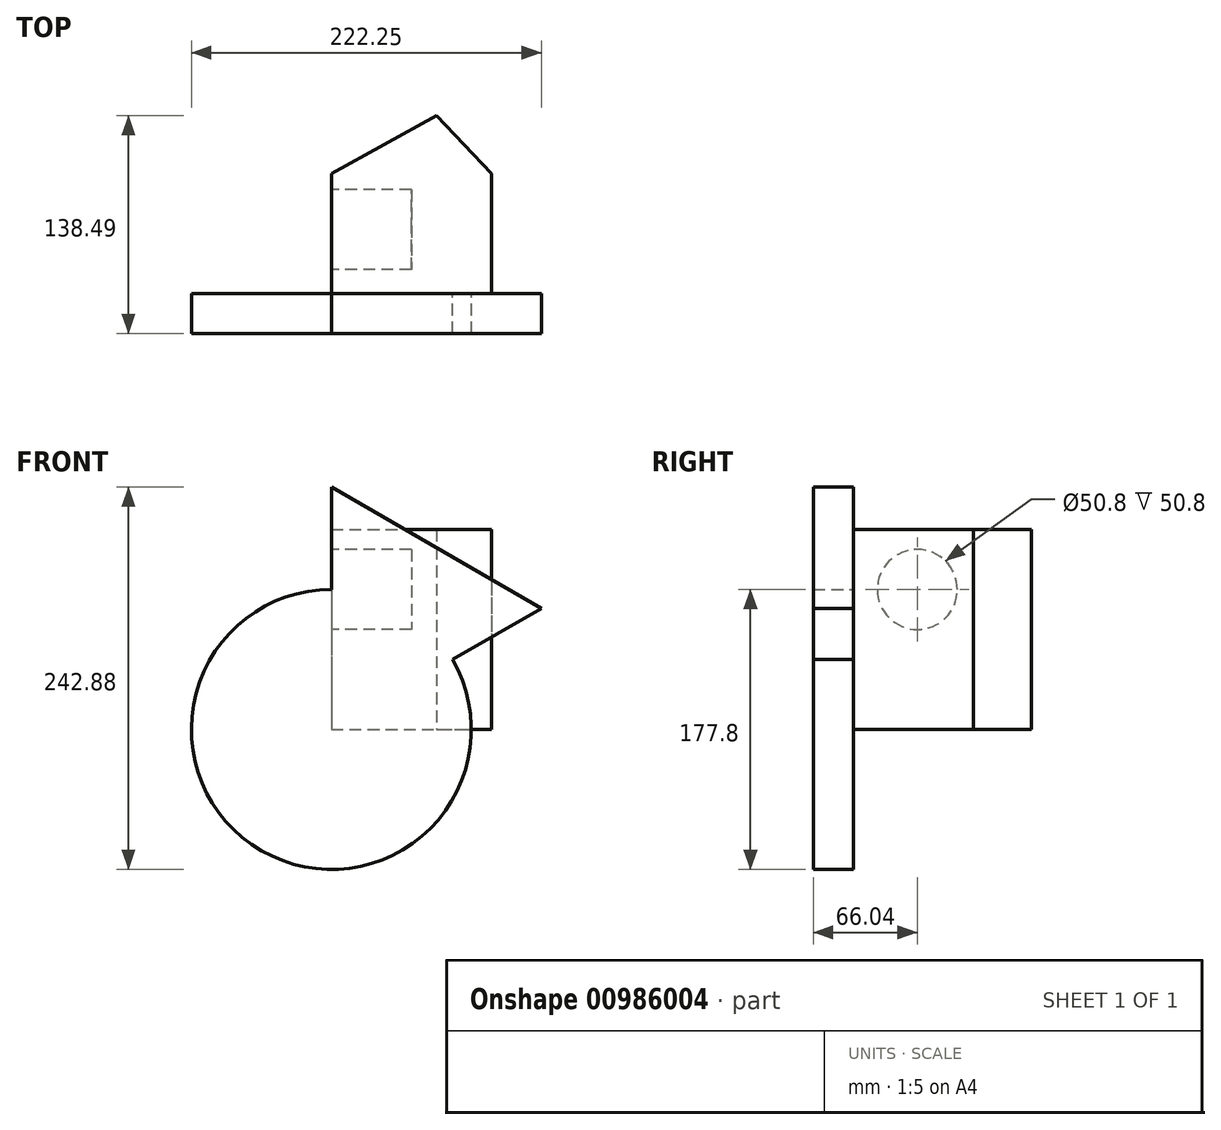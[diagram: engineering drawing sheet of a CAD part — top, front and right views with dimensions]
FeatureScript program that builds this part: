
annotation { "Feature Type Name" : "Feature", "Feature Type Description" : "" }
export const myFeature = defineFeature(function(context is Context, id is Id, definition is map)
    precondition{}
    {
        {
            var Q0;
            Q0=qCreatedBy(makeId("Front.planeOp"),FACE);
            var sketch = newSketch(context, id + "F0", { "sketchPlane" : qUnion([Q0])});
            skCircle(sketch, "E0", {"center": v(0, 0) * mm, "radius": 88.9 * mm});
            skCircle(sketch, "E1.cCircle", {"center": v(44.45, 76.99) * mm, "radius": 44.45 * mm, "construction": true});
            skLineSegment(sketch, "E1.0", {"start": v(133.35, 76.99) * mm, "end": v(0, 0) * mm});
            skLineSegment(sketch, "E1.1", {"start": v(0, 0) * mm, "end": v(0, 153.98) * mm});
            skLineSegment(sketch, "E1.2", {"start": v(0, 153.98) * mm, "end": v(133.35, 76.99) * mm});
            skPoint(sketch, "E1.0.midPoint", {"position": v(66.67, 38.5) * mm});
            skSolve(sketch);
        }
        {
            var Q0;
            Q0=qCreatedBy(makeId("Top.planeOp"),FACE);
            var sketch = newSketch(context, id + "F1", { "sketchPlane" : qUnion([Q0])});
            skLineSegment(sketch, "E2.bottom", {"start": v(0, 0) * mm, "end": v(101.6, 0) * mm});
            skLineSegment(sketch, "E2.top", {"start": v(0, 76.2) * mm, "end": v(101.6, 76.2) * mm});
            skLineSegment(sketch, "E2.left", {"start": v(0, 0) * mm, "end": v(0, 76.2) * mm});
            skLineSegment(sketch, "E2.right", {"start": v(101.6, 0) * mm, "end": v(101.6, 76.2) * mm});
            skLineSegment(sketch, "E3", {"start": v(0, 76.2) * mm, "end": v(66.68, 113.1) * mm});
            skLineSegment(sketch, "E4", {"start": v(66.68, 113.1) * mm, "end": v(101.6, 76.2) * mm});
            skSolve(sketch);
        }
        {
            var Q0;
            Q0 = qSketchRegion(id + "F1", true);
            extrude(context, id + "F2", {"entities" : qUnion([Q0]), "depth" : 127 * mm, "offsetDistance" : 25.4 * mm});
        }
        {
            var Q0;
            Q0=makeQuery(id+"F2.opExtrude","SWEPT_FACE",FACE,{"disambiguationData":[OSD([sQuery(id+"F1.wireOp",EDGE,"E2.left")])]});
            var sketch = newSketch(context, id + "F3", { "sketchPlane" : qUnion([Q0])});
            skCircle(sketch, "E5", {"center": v(-40.64, 88.9) * mm, "radius": 25.4 * mm});
            skSolve(sketch);
        }
        {
            var Q0;
            Q0 = qSketchRegion(id + "F3", true);
            extrude(context, id + "F4", {"entities" : qUnion([Q0]), "operationType" : NewBodyOperationType.REMOVE, "oppositeDirection" : true, "depth" : 50.8 * mm, "offsetDistance" : 25.4 * mm});
        }
        {
            var Q0;
            Q0 = qSketchRegion(id + "F0", true);
            extrude(context, id + "F5", {"entities" : qUnion([Q0]), "depth" : 25.4 * mm, "offsetDistance" : 25.4 * mm});
        }
    });
